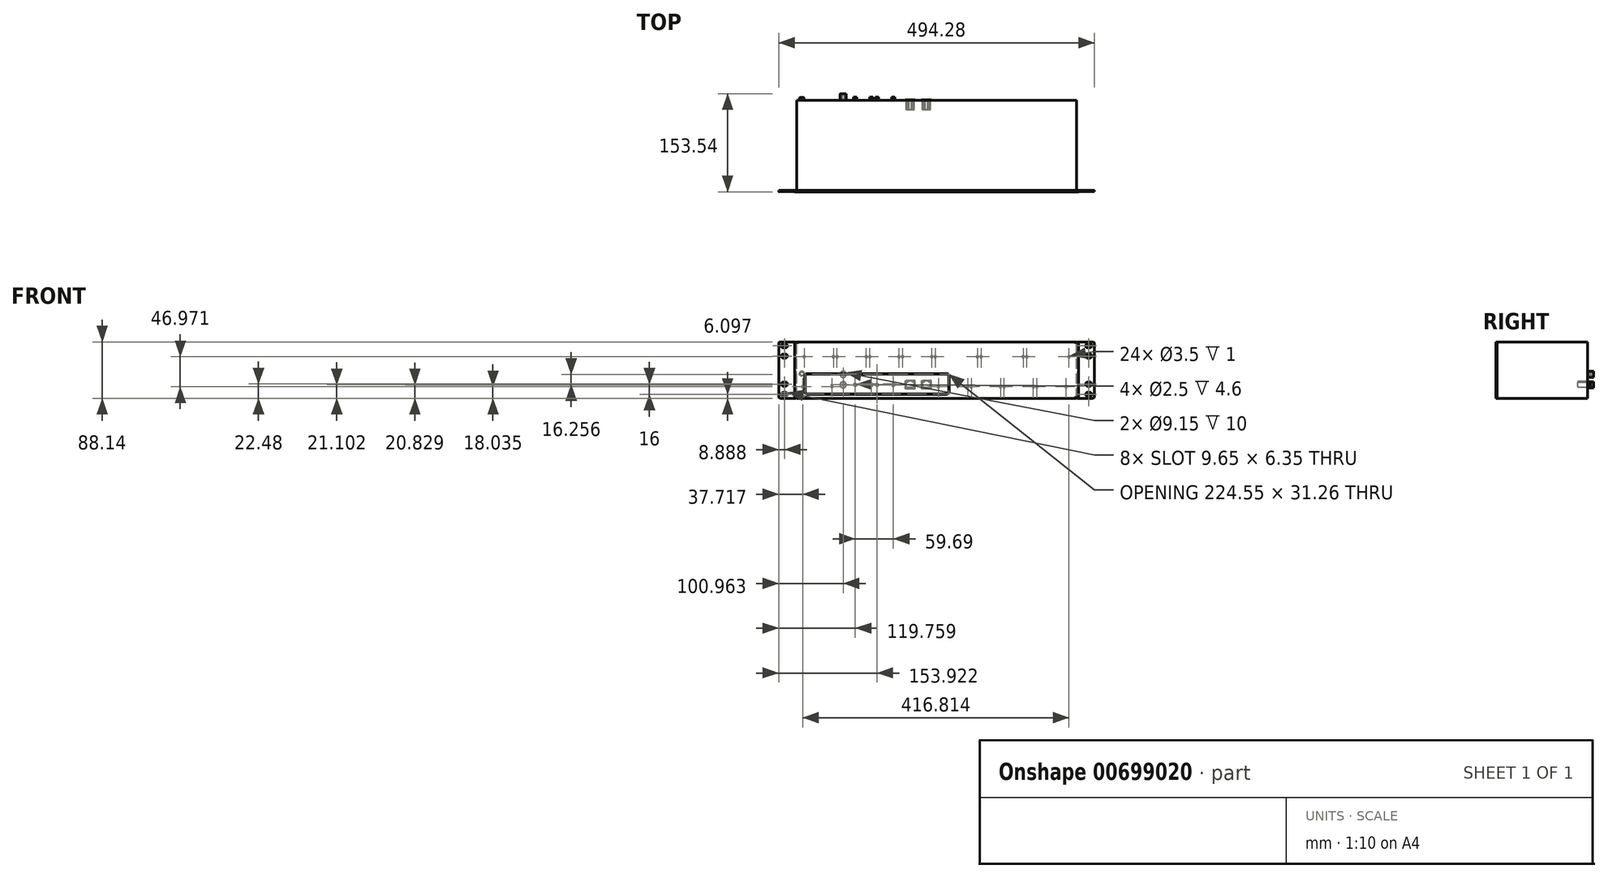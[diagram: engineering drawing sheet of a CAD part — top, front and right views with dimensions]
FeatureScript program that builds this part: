
annotation { "Feature Type Name" : "Feature", "Feature Type Description" : "" }
export const myFeature = defineFeature(function(context is Context, id is Id, definition is map)
    precondition{}
    {
        {
            var Q0;
            Q0=qCreatedBy(makeId("Front.planeOp"),FACE);
            var sketch = newSketch(context, id + "F0", { "sketchPlane" : qUnion([Q0])});
            skLineSegment(sketch, "E0.bottom", {"start": v(222.25, -44.07) * mm, "end": v(-222.25, -44.07) * mm});
            skLineSegment(sketch, "E0.top", {"start": v(222.25, 44.07) * mm, "end": v(-222.25, 44.07) * mm});
            skLineSegment(sketch, "E0.left", {"start": v(222.25, -44.07) * mm, "end": v(222.25, 44.07) * mm});
            skLineSegment(sketch, "E0.right", {"start": v(-222.25, -44.07) * mm, "end": v(-222.25, 44.07) * mm});
            skPoint(sketch, "E0.middle", {"position": v(0, 0) * mm});
            skPoint(sketch, "E1", {"position": v(-215.9, 44.07) * mm});
            skLineSegment(sketch, "E2", {"start": v(-215.9, 44.07) * mm, "end": v(-215.9, 43.3) * mm});
            skLineSegment(sketch, "E3", {"start": v(-215.9, 43.3) * mm, "end": v(-222.25, 43.3) * mm});
            skPoint(sketch, "E4.MirrorP", {"position": v(215.9, 44.07) * mm});
            skLineSegment(sketch, "E5.MirrorCS", {"start": v(215.9, 43.3) * mm, "end": v(222.25, 43.3) * mm});
            skLineSegment(sketch, "E6.MirrorCS", {"start": v(215.9, 44.07) * mm, "end": v(215.9, 43.3) * mm});
            skLineSegment(sketch, "E7.MirrorCS", {"start": v(-215.9, -44.07) * mm, "end": v(-215.9, -43.3) * mm});
            skLineSegment(sketch, "E8.MirrorCS", {"start": v(215.9, -44.07) * mm, "end": v(215.9, -43.3) * mm});
            skLineSegment(sketch, "E9.MirrorCS", {"start": v(-215.9, -43.3) * mm, "end": v(-222.25, -43.3) * mm});
            skLineSegment(sketch, "E10.MirrorCS", {"start": v(215.9, -43.3) * mm, "end": v(222.25, -43.3) * mm});
            skPoint(sketch, "E11.MirrorP", {"position": v(215.9, -44.07) * mm});
            skPoint(sketch, "E12.MirrorP", {"position": v(-215.9, -44.07) * mm});
            skPoint(sketch, "E13", {"position": v(-220.47, -44.07) * mm});
            skPoint(sketch, "E14", {"position": v(-220.47, 44.07) * mm});
            skLineSegment(sketch, "E15", {"start": v(-220.47, 44.07) * mm, "end": v(-247.14, 44.07) * mm});
            skLineSegment(sketch, "E16", {"start": v(-247.14, 44.07) * mm, "end": v(-247.14, -44.07) * mm});
            skLineSegment(sketch, "E17", {"start": v(-247.14, -44.07) * mm, "end": v(-220.47, -44.07) * mm});
            skPoint(sketch, "E18.MirrorP", {"position": v(220.47, 44.07) * mm});
            skLineSegment(sketch, "E19.MirrorCS", {"start": v(220.47, 44.07) * mm, "end": v(247.14, 44.07) * mm});
            skLineSegment(sketch, "E20.MirrorCS", {"start": v(247.14, 44.07) * mm, "end": v(247.14, -44.07) * mm});
            skLineSegment(sketch, "E21.MirrorCS", {"start": v(247.14, -44.07) * mm, "end": v(220.47, -44.07) * mm});
            skPoint(sketch, "E22.MirrorP", {"position": v(220.47, -44.07) * mm});
            skLineSegment(sketch, "E23", {"start": v(-220.47, 44.07) * mm, "end": v(-220.47, -44.07) * mm});
            skLineSegment(sketch, "E24", {"start": v(220.47, 44.07) * mm, "end": v(220.47, -44.07) * mm});
            skSolve(sketch);
        }
        {
            var Q0;
            {var subQ5=sQuery(id+"F0.wireOp",EDGE,"E2");Q0=makeQuery(id+"F0.imprint","IMPRINT",FACE,{"disambiguationData":[TD([[makeQuery(id+"F0.imprint","IMPRINT",EDGE,{"derivedFrom":subQ5}),1.0]])]});}
            var Q1;
            {var subQ0=sQuery(id+"F0.wireOp",EDGE,"E3");var subQ1=sQuery(id+"F0.wireOp",EDGE,"E0.right");var subQ2=makeQuery(id+"F0.imprint","INTERSECT",VERTEX,{"derivedFrom":[subQ1,subQ0]});Q1=makeQuery(id+"F0.imprint","IMPRINT",FACE,{"disambiguationData":[TD([[makeQuery(id+"F0.imprint","IMPRINT",EDGE,{"disambiguationData":[TD([[subQ2,1.0]])],"derivedFrom":subQ1}),-1.0]])]});}
            var Q2;
            {var subQ0=sQuery(id+"F0.wireOp",EDGE,"E5.MirrorCS");var subQ1=sQuery(id+"F0.wireOp",EDGE,"E0.left");var subQ2=makeQuery(id+"F0.imprint","INTERSECT",VERTEX,{"derivedFrom":[subQ1,subQ0]});Q2=makeQuery(id+"F0.imprint","IMPRINT",FACE,{"disambiguationData":[TD([[makeQuery(id+"F0.imprint","IMPRINT",EDGE,{"disambiguationData":[TD([[subQ2,1.0]])],"derivedFrom":subQ1}),1.0]])]});}
            extrude(context, id + "F1", {"entities" : qUnion([Q0, Q1, Q2]), "depth" : 2 * mm, "offsetDistance" : 25 * mm});
        }
        {
            var Q0;
            Q0=makeQuery(id+"F1.opExtrude","SWEPT_EDGE",EDGE,{"disambiguationData":[OSD([sQuery(id+"F0.wireOp",EDGE,"E0.right"),sQuery(id+"F0.wireOp",EDGE,"E3")])]});
            var Q1;
            Q1=makeQuery(id+"F1.opExtrude","SWEPT_EDGE",EDGE,{"disambiguationData":[OSD([sQuery(id+"F0.wireOp",EDGE,"E0.right"),sQuery(id+"F0.wireOp",EDGE,"E9.MirrorCS")])]});
            var Q2;
            Q2=makeQuery(id+"F1.opExtrude","SWEPT_EDGE",EDGE,{"disambiguationData":[OSD([sQuery(id+"F0.wireOp",EDGE,"E0.left"),sQuery(id+"F0.wireOp",EDGE,"E10.MirrorCS")])]});
            var Q3;
            Q3=makeQuery(id+"F1.opExtrude","SWEPT_EDGE",EDGE,{"disambiguationData":[OSD([sQuery(id+"F0.wireOp",EDGE,"E0.left"),sQuery(id+"F0.wireOp",EDGE,"E5.MirrorCS")])]});
            fillet(context, id + "F2", {"entities" : qUnion([Q0, Q1, Q2, Q3]), "radius" : 3 * mm, "tangentPropagation" : true, "allowEdgeOverflow" : false});
        }
        {
            var Q0;
            {var subQ3=sQuery(id+"F0.wireOp",EDGE,"E16");Q0=makeQuery(id+"F0.imprint","IMPRINT",FACE,{"disambiguationData":[TD([[makeQuery(id+"F0.imprint","IMPRINT",EDGE,{"derivedFrom":subQ3}),1.0]])]});}
            var Q1;
            {var subQ0=sQuery(id+"F0.wireOp",EDGE,"E15");var subQ1=sQuery(id+"F0.wireOp",EDGE,"E0.right");var subQ2=makeQuery(id+"F0.imprint","INTERSECT",VERTEX,{"derivedFrom":[subQ1,subQ0]});Q1=makeQuery(id+"F0.imprint","IMPRINT",FACE,{"disambiguationData":[TD([[makeQuery(id+"F0.imprint","IMPRINT",EDGE,{"disambiguationData":[TD([[subQ2,1.0]])],"derivedFrom":subQ1}),-1.0]])]});}
            var Q2;
            {var subQ0=sQuery(id+"F0.wireOp",EDGE,"E3");var subQ1=sQuery(id+"F0.wireOp",EDGE,"E0.right");var subQ2=makeQuery(id+"F0.imprint","INTERSECT",VERTEX,{"derivedFrom":[subQ1,subQ0]});Q2=makeQuery(id+"F0.imprint","IMPRINT",FACE,{"disambiguationData":[TD([[makeQuery(id+"F0.imprint","IMPRINT",EDGE,{"disambiguationData":[TD([[subQ2,1.0]])],"derivedFrom":subQ1}),-1.0]])]});}
            var Q3;
            {var subQ0=sQuery(id+"F0.wireOp",EDGE,"E17");var subQ1=sQuery(id+"F0.wireOp",EDGE,"E0.right");var subQ2=makeQuery(id+"F0.imprint","INTERSECT",VERTEX,{"derivedFrom":[subQ1,subQ0]});Q3=makeQuery(id+"F0.imprint","IMPRINT",FACE,{"disambiguationData":[TD([[makeQuery(id+"F0.imprint","IMPRINT",EDGE,{"disambiguationData":[TD([[subQ2,-1.0]])],"derivedFrom":subQ1}),-1.0]])]});}
            var Q4;
            {var subQ3=sQuery(id+"F0.wireOp",EDGE,"E20.MirrorCS");Q4=makeQuery(id+"F0.imprint","IMPRINT",FACE,{"disambiguationData":[TD([[makeQuery(id+"F0.imprint","IMPRINT",EDGE,{"derivedFrom":subQ3}),-1.0]])]});}
            var Q5;
            {var subQ0=sQuery(id+"F0.wireOp",EDGE,"E19.MirrorCS");var subQ1=sQuery(id+"F0.wireOp",EDGE,"E0.left");var subQ2=makeQuery(id+"F0.imprint","INTERSECT",VERTEX,{"derivedFrom":[subQ1,subQ0]});Q5=makeQuery(id+"F0.imprint","IMPRINT",FACE,{"disambiguationData":[TD([[makeQuery(id+"F0.imprint","IMPRINT",EDGE,{"disambiguationData":[TD([[subQ2,1.0]])],"derivedFrom":subQ1}),1.0]])]});}
            var Q6;
            {var subQ0=sQuery(id+"F0.wireOp",EDGE,"E5.MirrorCS");var subQ1=sQuery(id+"F0.wireOp",EDGE,"E0.left");var subQ2=makeQuery(id+"F0.imprint","INTERSECT",VERTEX,{"derivedFrom":[subQ1,subQ0]});Q6=makeQuery(id+"F0.imprint","IMPRINT",FACE,{"disambiguationData":[TD([[makeQuery(id+"F0.imprint","IMPRINT",EDGE,{"disambiguationData":[TD([[subQ2,1.0]])],"derivedFrom":subQ1}),1.0]])]});}
            var Q7;
            {var subQ0=sQuery(id+"F0.wireOp",EDGE,"E21.MirrorCS");var subQ1=sQuery(id+"F0.wireOp",EDGE,"E0.left");var subQ2=makeQuery(id+"F0.imprint","INTERSECT",VERTEX,{"derivedFrom":[subQ1,subQ0]});Q7=makeQuery(id+"F0.imprint","IMPRINT",FACE,{"disambiguationData":[TD([[makeQuery(id+"F0.imprint","IMPRINT",EDGE,{"disambiguationData":[TD([[subQ2,-1.0]])],"derivedFrom":subQ1}),1.0]])]});}
            extrude(context, id + "F3", {"entities" : qUnion([Q0, Q1, Q2, Q3, Q4, Q5, Q6, Q7]), "depth" : 1.9 * mm, "offsetDistance" : 25 * mm});
        }
        {
            var Q0;
            Q0=makeQuery(id+"F3.opExtrude","SWEPT_EDGE",EDGE,{"disambiguationData":[OSD([sQuery(id+"F0.wireOp",EDGE,"E15"),sQuery(id+"F0.wireOp",EDGE,"E16")])]});
            var Q1;
            Q1=makeQuery(id+"F3.opExtrude","SWEPT_EDGE",EDGE,{"disambiguationData":[OSD([sQuery(id+"F0.wireOp",EDGE,"E16"),sQuery(id+"F0.wireOp",EDGE,"E17")])]});
            var Q2;
            Q2=makeQuery(id+"F3.opExtrude","SWEPT_EDGE",EDGE,{"disambiguationData":[OSD([sQuery(id+"F0.wireOp",EDGE,"E20.MirrorCS"),sQuery(id+"F0.wireOp",EDGE,"E21.MirrorCS")])]});
            var Q3;
            Q3=makeQuery(id+"F3.opExtrude","SWEPT_EDGE",EDGE,{"disambiguationData":[OSD([sQuery(id+"F0.wireOp",EDGE,"E19.MirrorCS"),sQuery(id+"F0.wireOp",EDGE,"E20.MirrorCS")])]});
            fillet(context, id + "F4", {"entities" : qUnion([Q0, Q1, Q2, Q3]), "radius" : 2.5 * mm, "tangentPropagation" : true, "allowEdgeOverflow" : false});
        }
        {
            var Q0;
            Q0=makeQuery(id+"F3.opExtrude","CAP_FACE",FACE,{"disambiguationData":[OSD([sQuery(id+"F0.wireOp",EDGE,"E15"),sQuery(id+"F0.wireOp",EDGE,"E16"),sQuery(id+"F0.wireOp",EDGE,"E17"),sQuery(id+"F0.wireOp",EDGE,"E23")])],"isStart":false});
            var sketch = newSketch(context, id + "F5", { "sketchPlane" : qUnion([Q0])});
            skLineSegment(sketch, "E25", {"start": v(-239.9, -41.15) * mm, "end": v(-236.6, -41.15) * mm});
            skLineSegment(sketch, "E26", {"start": v(-236.6, -41.15) * mm, "end": v(-236.6, -34.8) * mm});
            skLineSegment(sketch, "E27", {"start": v(-236.6, -34.8) * mm, "end": v(-239.9, -34.8) * mm});
            skLineSegment(sketch, "E28", {"start": v(-239.9, -34.8) * mm, "end": v(-239.9, -41.15) * mm});
            skLineSegment(sketch, "E29", {"start": v(-239.9, -37.97) * mm, "end": v(-243.08, -37.97) * mm});
            skLineSegment(sketch, "E30", {"start": v(-236.6, -37.97) * mm, "end": v(-233.43, -37.97) * mm});
            skArc(sketch, "E31", {"start": v(-239.9, -34.8) * mm, "mid": v(-243.08, -37.97) * mm, "end": v(-239.9, -41.15) * mm});
            skArc(sketch, "E32", {"start": v(-236.6, -41.15) * mm, "mid": v(-233.43, -37.97) * mm, "end": v(-236.6, -34.8) * mm});
            skPoint(sketch, "E33", {"position": v(-238.25, -34.8) * mm});
            skLineSegment(sketch, "E34.0.1.0", {"start": v(-239.9, -18.8) * mm, "end": v(-239.9, -25.15) * mm});
            skLineSegment(sketch, "E34.0.1.1", {"start": v(-239.9, -21.97) * mm, "end": v(-243.08, -21.97) * mm});
            skLineSegment(sketch, "E34.0.1.2", {"start": v(-236.6, -21.97) * mm, "end": v(-233.43, -21.97) * mm});
            skArc(sketch, "E34.0.1.3", {"start": v(-239.9, -18.8) * mm, "mid": v(-243.08, -21.97) * mm, "end": v(-239.9, -25.15) * mm});
            skArc(sketch, "E34.0.1.4", {"start": v(-236.6, -25.15) * mm, "mid": v(-233.43, -21.97) * mm, "end": v(-236.6, -18.8) * mm});
            skLineSegment(sketch, "E34.0.1.5", {"start": v(-236.6, -25.15) * mm, "end": v(-236.6, -18.8) * mm});
            skLineSegment(sketch, "E34.0.1.6", {"start": v(-239.9, -25.15) * mm, "end": v(-236.6, -25.15) * mm});
            skPoint(sketch, "E34.0.1.7", {"position": v(-238.25, -18.8) * mm});
            skLineSegment(sketch, "E34.0.1.8", {"start": v(-236.6, -18.8) * mm, "end": v(-239.9, -18.8) * mm});
            skLineSegment(sketch, "E34.direction1", {"start": v(-239.9, -41.15) * mm, "end": v(-214.9, -41.15) * mm, "construction": true});
            skLineSegment(sketch, "E34.direction2", {"start": v(-239.9, -41.15) * mm, "end": v(-239.9, -25.15) * mm, "construction": true});
            skLineSegment(sketch, "E35.MirrorCS", {"start": v(-236.6, 21.97) * mm, "end": v(-233.43, 21.97) * mm});
            skLineSegment(sketch, "E36.MirrorCS", {"start": v(-239.9, 21.97) * mm, "end": v(-243.08, 21.97) * mm});
            skLineSegment(sketch, "E37.MirrorCS", {"start": v(-239.9, 18.8) * mm, "end": v(-239.9, 25.15) * mm});
            skLineSegment(sketch, "E38.MirrorCS", {"start": v(-236.6, 37.97) * mm, "end": v(-233.43, 37.97) * mm});
            skLineSegment(sketch, "E39.MirrorCS", {"start": v(-236.6, 18.8) * mm, "end": v(-239.9, 18.8) * mm});
            skLineSegment(sketch, "E40.MirrorCS", {"start": v(-239.9, 37.97) * mm, "end": v(-243.08, 37.97) * mm});
            skLineSegment(sketch, "E41.MirrorCS", {"start": v(-239.9, 41.15) * mm, "end": v(-236.6, 41.15) * mm});
            skLineSegment(sketch, "E42.MirrorCS", {"start": v(-236.6, 34.8) * mm, "end": v(-239.9, 34.8) * mm});
            skLineSegment(sketch, "E43.MirrorCS", {"start": v(-239.9, 34.8) * mm, "end": v(-239.9, 41.15) * mm});
            skLineSegment(sketch, "E44.MirrorCS", {"start": v(-236.6, 41.15) * mm, "end": v(-236.6, 34.8) * mm});
            skLineSegment(sketch, "E45.MirrorCS", {"start": v(-239.9, 41.15) * mm, "end": v(-239.9, 25.15) * mm, "construction": true});
            skPoint(sketch, "E46.MirrorP", {"position": v(-238.25, 18.8) * mm});
            skArc(sketch, "E47.MirrorCS", {"start": v(-236.6, 25.15) * mm, "mid": v(-233.43, 21.97) * mm, "end": v(-236.6, 18.8) * mm});
            skArc(sketch, "E48.MirrorCS", {"start": v(-239.9, 18.8) * mm, "mid": v(-243.08, 21.97) * mm, "end": v(-239.9, 25.15) * mm});
            skArc(sketch, "E49.MirrorCS", {"start": v(-236.6, 41.15) * mm, "mid": v(-233.43, 37.97) * mm, "end": v(-236.6, 34.8) * mm});
            skPoint(sketch, "E50.MirrorP", {"position": v(-238.25, 34.8) * mm});
            skArc(sketch, "E51.MirrorCS", {"start": v(-239.9, 34.8) * mm, "mid": v(-243.08, 37.97) * mm, "end": v(-239.9, 41.15) * mm});
            skLineSegment(sketch, "E52.MirrorCS", {"start": v(-236.6, 25.15) * mm, "end": v(-236.6, 18.8) * mm});
            skLineSegment(sketch, "E53.MirrorCS", {"start": v(-239.9, 25.15) * mm, "end": v(-236.6, 25.15) * mm});
            skLineSegment(sketch, "E54.MirrorCS", {"start": v(236.6, -41.15) * mm, "end": v(236.6, -34.8) * mm});
            skLineSegment(sketch, "E55.MirrorCS", {"start": v(236.6, -34.8) * mm, "end": v(239.9, -34.8) * mm});
            skLineSegment(sketch, "E56.MirrorCS", {"start": v(239.9, -34.8) * mm, "end": v(239.9, -41.15) * mm});
            skLineSegment(sketch, "E57.MirrorCS", {"start": v(239.9, -37.97) * mm, "end": v(243.08, -37.97) * mm});
            skPoint(sketch, "E58.MirrorP", {"position": v(238.25, -34.8) * mm});
            skLineSegment(sketch, "E59.MirrorCS", {"start": v(236.6, -37.97) * mm, "end": v(233.43, -37.97) * mm});
            skLineSegment(sketch, "E60.MirrorCS", {"start": v(239.9, -41.15) * mm, "end": v(236.6, -41.15) * mm});
            skArc(sketch, "E61.MirrorCS", {"start": v(239.9, -34.8) * mm, "mid": v(243.08, -37.97) * mm, "end": v(239.9, -41.15) * mm});
            skArc(sketch, "E62.MirrorCS", {"start": v(236.6, -41.15) * mm, "mid": v(233.43, -37.97) * mm, "end": v(236.6, -34.8) * mm});
            skArc(sketch, "E63.0.1.0", {"start": v(236.6, -25.15) * mm, "mid": v(233.43, -21.97) * mm, "end": v(236.6, -18.8) * mm});
            skLineSegment(sketch, "E63.0.1.1", {"start": v(239.9, -21.97) * mm, "end": v(243.08, -21.97) * mm});
            skLineSegment(sketch, "E63.0.1.2", {"start": v(239.9, -18.8) * mm, "end": v(239.9, -25.15) * mm});
            skLineSegment(sketch, "E63.0.1.3", {"start": v(236.6, -25.15) * mm, "end": v(236.6, -18.8) * mm});
            skArc(sketch, "E63.0.1.4", {"start": v(239.9, -18.8) * mm, "mid": v(243.08, -21.97) * mm, "end": v(239.9, -25.15) * mm});
            skPoint(sketch, "E63.0.1.5", {"position": v(238.25, -18.8) * mm});
            skLineSegment(sketch, "E63.0.1.6", {"start": v(239.9, -25.15) * mm, "end": v(236.6, -25.15) * mm});
            skLineSegment(sketch, "E63.0.1.7", {"start": v(236.6, -21.97) * mm, "end": v(233.43, -21.97) * mm});
            skLineSegment(sketch, "E63.0.1.8", {"start": v(236.6, -18.8) * mm, "end": v(239.9, -18.8) * mm});
            skLineSegment(sketch, "E63.direction1", {"start": v(236.6, -41.15) * mm, "end": v(261.6, -41.15) * mm, "construction": true});
            skLineSegment(sketch, "E63.direction2", {"start": v(236.6, -41.15) * mm, "end": v(236.6, -25.15) * mm, "construction": true});
            skLineSegment(sketch, "E64.MirrorCS", {"start": v(236.6, 34.8) * mm, "end": v(239.9, 34.8) * mm});
            skLineSegment(sketch, "E65.MirrorCS", {"start": v(236.6, 18.8) * mm, "end": v(239.9, 18.8) * mm});
            skLineSegment(sketch, "E66.MirrorCS", {"start": v(236.6, 41.15) * mm, "end": v(236.6, 34.8) * mm});
            skArc(sketch, "E67.MirrorCS", {"start": v(239.9, 18.8) * mm, "mid": v(243.08, 21.97) * mm, "end": v(239.9, 25.15) * mm});
            skLineSegment(sketch, "E68.MirrorCS", {"start": v(239.9, 37.97) * mm, "end": v(243.08, 37.97) * mm});
            skLineSegment(sketch, "E69.MirrorCS", {"start": v(236.6, 41.15) * mm, "end": v(236.6, 25.15) * mm, "construction": true});
            skLineSegment(sketch, "E70.MirrorCS", {"start": v(239.9, 18.8) * mm, "end": v(239.9, 25.15) * mm});
            skArc(sketch, "E71.MirrorCS", {"start": v(239.9, 34.8) * mm, "mid": v(243.08, 37.97) * mm, "end": v(239.9, 41.15) * mm});
            skLineSegment(sketch, "E72.MirrorCS", {"start": v(239.9, 34.8) * mm, "end": v(239.9, 41.15) * mm});
            skArc(sketch, "E73.MirrorCS", {"start": v(236.6, 25.15) * mm, "mid": v(233.43, 21.97) * mm, "end": v(236.6, 18.8) * mm});
            skLineSegment(sketch, "E74.MirrorCS", {"start": v(239.9, 21.97) * mm, "end": v(243.08, 21.97) * mm});
            skLineSegment(sketch, "E75.MirrorCS", {"start": v(236.6, 25.15) * mm, "end": v(236.6, 18.8) * mm});
            skPoint(sketch, "E76.MirrorP", {"position": v(238.25, 18.8) * mm});
            skPoint(sketch, "E77.MirrorP", {"position": v(238.25, 34.8) * mm});
            skLineSegment(sketch, "E78.MirrorCS", {"start": v(236.6, 21.97) * mm, "end": v(233.43, 21.97) * mm});
            skLineSegment(sketch, "E79.MirrorCS", {"start": v(239.9, 41.15) * mm, "end": v(236.6, 41.15) * mm});
            skArc(sketch, "E80.MirrorCS", {"start": v(236.6, 41.15) * mm, "mid": v(233.43, 37.97) * mm, "end": v(236.6, 34.8) * mm});
            skLineSegment(sketch, "E81.MirrorCS", {"start": v(239.9, 25.15) * mm, "end": v(236.6, 25.15) * mm});
            skLineSegment(sketch, "E82.MirrorCS", {"start": v(236.6, 37.97) * mm, "end": v(233.43, 37.97) * mm});
            skSolve(sketch);
        }
        {
            var Q0;
            {var subQ0=sQuery(id+"F5.wireOp",EDGE,"E40.MirrorCS");Q0=makeQuery(id+"F5.imprint","IMPRINT",FACE,{"disambiguationData":[TD([[makeQuery(id+"F5.imprint","IMPRINT",EDGE,{"derivedFrom":subQ0}),-1.0]])]});}
            var Q1;
            {var subQ0=sQuery(id+"F5.wireOp",EDGE,"E40.MirrorCS");Q1=makeQuery(id+"F5.imprint","IMPRINT",FACE,{"disambiguationData":[TD([[makeQuery(id+"F5.imprint","IMPRINT",EDGE,{"derivedFrom":subQ0}),1.0]])]});}
            var Q2;
            {var subQ3=sQuery(id+"F5.wireOp",EDGE,"E41.MirrorCS");Q2=makeQuery(id+"F5.imprint","IMPRINT",FACE,{"disambiguationData":[TD([[makeQuery(id+"F5.imprint","IMPRINT",EDGE,{"derivedFrom":subQ3}),-1.0]])]});}
            var Q3;
            {var subQ0=sQuery(id+"F5.wireOp",EDGE,"E38.MirrorCS");Q3=makeQuery(id+"F5.imprint","IMPRINT",FACE,{"disambiguationData":[TD([[makeQuery(id+"F5.imprint","IMPRINT",EDGE,{"derivedFrom":subQ0}),-1.0]])]});}
            var Q4;
            {var subQ0=sQuery(id+"F5.wireOp",EDGE,"E38.MirrorCS");Q4=makeQuery(id+"F5.imprint","IMPRINT",FACE,{"disambiguationData":[TD([[makeQuery(id+"F5.imprint","IMPRINT",EDGE,{"derivedFrom":subQ0}),1.0]])]});}
            var Q5;
            {var subQ0=sQuery(id+"F5.wireOp",EDGE,"E36.MirrorCS");Q5=makeQuery(id+"F5.imprint","IMPRINT",FACE,{"disambiguationData":[TD([[makeQuery(id+"F5.imprint","IMPRINT",EDGE,{"derivedFrom":subQ0}),-1.0]])]});}
            var Q6;
            {var subQ0=sQuery(id+"F5.wireOp",EDGE,"E36.MirrorCS");Q6=makeQuery(id+"F5.imprint","IMPRINT",FACE,{"disambiguationData":[TD([[makeQuery(id+"F5.imprint","IMPRINT",EDGE,{"derivedFrom":subQ0}),1.0]])]});}
            var Q7;
            {var subQ4=sQuery(id+"F5.wireOp",EDGE,"E39.MirrorCS");Q7=makeQuery(id+"F5.imprint","IMPRINT",FACE,{"disambiguationData":[TD([[makeQuery(id+"F5.imprint","IMPRINT",EDGE,{"derivedFrom":subQ4}),-1.0]])]});}
            var Q8;
            {var subQ0=sQuery(id+"F5.wireOp",EDGE,"E35.MirrorCS");Q8=makeQuery(id+"F5.imprint","IMPRINT",FACE,{"disambiguationData":[TD([[makeQuery(id+"F5.imprint","IMPRINT",EDGE,{"derivedFrom":subQ0}),-1.0]])]});}
            var Q9;
            {var subQ0=sQuery(id+"F5.wireOp",EDGE,"E35.MirrorCS");Q9=makeQuery(id+"F5.imprint","IMPRINT",FACE,{"disambiguationData":[TD([[makeQuery(id+"F5.imprint","IMPRINT",EDGE,{"derivedFrom":subQ0}),1.0]])]});}
            var Q10;
            {var subQ3=sQuery(id+"F5.wireOp",EDGE,"E29");Q10=makeQuery(id+"F5.imprint","IMPRINT",FACE,{"disambiguationData":[TD([[makeQuery(id+"F5.imprint","IMPRINT",EDGE,{"derivedFrom":subQ3}),-1.0]])]});}
            var Q11;
            {var subQ3=sQuery(id+"F5.wireOp",EDGE,"E29");Q11=makeQuery(id+"F5.imprint","IMPRINT",FACE,{"disambiguationData":[TD([[makeQuery(id+"F5.imprint","IMPRINT",EDGE,{"derivedFrom":subQ3}),1.0]])]});}
            var Q12;
            {var subQ4=sQuery(id+"F5.wireOp",EDGE,"E25");Q12=makeQuery(id+"F5.imprint","IMPRINT",FACE,{"disambiguationData":[TD([[makeQuery(id+"F5.imprint","IMPRINT",EDGE,{"derivedFrom":subQ4}),1.0]])]});}
            var Q13;
            {var subQ3=sQuery(id+"F5.wireOp",EDGE,"E30");Q13=makeQuery(id+"F5.imprint","IMPRINT",FACE,{"disambiguationData":[TD([[makeQuery(id+"F5.imprint","IMPRINT",EDGE,{"derivedFrom":subQ3}),-1.0]])]});}
            var Q14;
            {var subQ3=sQuery(id+"F5.wireOp",EDGE,"E30");Q14=makeQuery(id+"F5.imprint","IMPRINT",FACE,{"disambiguationData":[TD([[makeQuery(id+"F5.imprint","IMPRINT",EDGE,{"derivedFrom":subQ3}),1.0]])]});}
            var Q15;
            {var subQ0=sQuery(id+"F5.wireOp",EDGE,"E34.0.1.2");Q15=makeQuery(id+"F5.imprint","IMPRINT",FACE,{"disambiguationData":[TD([[makeQuery(id+"F5.imprint","IMPRINT",EDGE,{"derivedFrom":subQ0}),1.0]])]});}
            var Q16;
            {var subQ0=sQuery(id+"F5.wireOp",EDGE,"E34.0.1.2");Q16=makeQuery(id+"F5.imprint","IMPRINT",FACE,{"disambiguationData":[TD([[makeQuery(id+"F5.imprint","IMPRINT",EDGE,{"derivedFrom":subQ0}),-1.0]])]});}
            var Q17;
            {var subQ4=sQuery(id+"F5.wireOp",EDGE,"E34.0.1.6");Q17=makeQuery(id+"F5.imprint","IMPRINT",FACE,{"disambiguationData":[TD([[makeQuery(id+"F5.imprint","IMPRINT",EDGE,{"derivedFrom":subQ4}),1.0]])]});}
            var Q18;
            {var subQ3=sQuery(id+"F5.wireOp",EDGE,"E34.0.1.1");Q18=makeQuery(id+"F5.imprint","IMPRINT",FACE,{"disambiguationData":[TD([[makeQuery(id+"F5.imprint","IMPRINT",EDGE,{"derivedFrom":subQ3}),1.0]])]});}
            var Q19;
            {var subQ3=sQuery(id+"F5.wireOp",EDGE,"E34.0.1.1");Q19=makeQuery(id+"F5.imprint","IMPRINT",FACE,{"disambiguationData":[TD([[makeQuery(id+"F5.imprint","IMPRINT",EDGE,{"derivedFrom":subQ3}),-1.0]])]});}
            var Q20;
            {var subQ3=sQuery(id+"F5.wireOp",EDGE,"E82.MirrorCS");Q20=makeQuery(id+"F5.imprint","IMPRINT",FACE,{"disambiguationData":[TD([[makeQuery(id+"F5.imprint","IMPRINT",EDGE,{"derivedFrom":subQ3}),-1.0]])]});}
            var Q21;
            {var subQ3=sQuery(id+"F5.wireOp",EDGE,"E82.MirrorCS");Q21=makeQuery(id+"F5.imprint","IMPRINT",FACE,{"disambiguationData":[TD([[makeQuery(id+"F5.imprint","IMPRINT",EDGE,{"derivedFrom":subQ3}),1.0]])]});}
            var Q22;
            {var subQ2=sQuery(id+"F5.wireOp",EDGE,"E64.MirrorCS");Q22=makeQuery(id+"F5.imprint","IMPRINT",FACE,{"disambiguationData":[TD([[makeQuery(id+"F5.imprint","IMPRINT",EDGE,{"derivedFrom":subQ2}),1.0]])]});}
            var Q23;
            {var subQ0=sQuery(id+"F5.wireOp",EDGE,"E68.MirrorCS");Q23=makeQuery(id+"F5.imprint","IMPRINT",FACE,{"disambiguationData":[TD([[makeQuery(id+"F5.imprint","IMPRINT",EDGE,{"derivedFrom":subQ0}),1.0]])]});}
            var Q24;
            {var subQ0=sQuery(id+"F5.wireOp",EDGE,"E68.MirrorCS");Q24=makeQuery(id+"F5.imprint","IMPRINT",FACE,{"disambiguationData":[TD([[makeQuery(id+"F5.imprint","IMPRINT",EDGE,{"derivedFrom":subQ0}),-1.0]])]});}
            var Q25;
            {var subQ3=sQuery(id+"F5.wireOp",EDGE,"E78.MirrorCS");Q25=makeQuery(id+"F5.imprint","IMPRINT",FACE,{"disambiguationData":[TD([[makeQuery(id+"F5.imprint","IMPRINT",EDGE,{"derivedFrom":subQ3}),-1.0]])]});}
            var Q26;
            {var subQ3=sQuery(id+"F5.wireOp",EDGE,"E78.MirrorCS");Q26=makeQuery(id+"F5.imprint","IMPRINT",FACE,{"disambiguationData":[TD([[makeQuery(id+"F5.imprint","IMPRINT",EDGE,{"derivedFrom":subQ3}),1.0]])]});}
            var Q27;
            {var subQ4=sQuery(id+"F5.wireOp",EDGE,"E65.MirrorCS");Q27=makeQuery(id+"F5.imprint","IMPRINT",FACE,{"disambiguationData":[TD([[makeQuery(id+"F5.imprint","IMPRINT",EDGE,{"derivedFrom":subQ4}),1.0]])]});}
            var Q28;
            {var subQ3=sQuery(id+"F5.wireOp",EDGE,"E74.MirrorCS");Q28=makeQuery(id+"F5.imprint","IMPRINT",FACE,{"disambiguationData":[TD([[makeQuery(id+"F5.imprint","IMPRINT",EDGE,{"derivedFrom":subQ3}),1.0]])]});}
            var Q29;
            {var subQ3=sQuery(id+"F5.wireOp",EDGE,"E74.MirrorCS");Q29=makeQuery(id+"F5.imprint","IMPRINT",FACE,{"disambiguationData":[TD([[makeQuery(id+"F5.imprint","IMPRINT",EDGE,{"derivedFrom":subQ3}),-1.0]])]});}
            var Q30;
            {var subQ3=sQuery(id+"F5.wireOp",EDGE,"E63.0.1.7");Q30=makeQuery(id+"F5.imprint","IMPRINT",FACE,{"disambiguationData":[TD([[makeQuery(id+"F5.imprint","IMPRINT",EDGE,{"derivedFrom":subQ3}),-1.0]])]});}
            var Q31;
            {var subQ3=sQuery(id+"F5.wireOp",EDGE,"E63.0.1.7");Q31=makeQuery(id+"F5.imprint","IMPRINT",FACE,{"disambiguationData":[TD([[makeQuery(id+"F5.imprint","IMPRINT",EDGE,{"derivedFrom":subQ3}),1.0]])]});}
            var Q32;
            {var subQ4=sQuery(id+"F5.wireOp",EDGE,"E63.0.1.6");Q32=makeQuery(id+"F5.imprint","IMPRINT",FACE,{"disambiguationData":[TD([[makeQuery(id+"F5.imprint","IMPRINT",EDGE,{"derivedFrom":subQ4}),-1.0]])]});}
            var Q33;
            {var subQ0=sQuery(id+"F5.wireOp",EDGE,"E63.0.1.1");Q33=makeQuery(id+"F5.imprint","IMPRINT",FACE,{"disambiguationData":[TD([[makeQuery(id+"F5.imprint","IMPRINT",EDGE,{"derivedFrom":subQ0}),1.0]])]});}
            var Q34;
            {var subQ0=sQuery(id+"F5.wireOp",EDGE,"E63.0.1.1");Q34=makeQuery(id+"F5.imprint","IMPRINT",FACE,{"disambiguationData":[TD([[makeQuery(id+"F5.imprint","IMPRINT",EDGE,{"derivedFrom":subQ0}),-1.0]])]});}
            var Q35;
            {var subQ3=sQuery(id+"F5.wireOp",EDGE,"E59.MirrorCS");Q35=makeQuery(id+"F5.imprint","IMPRINT",FACE,{"disambiguationData":[TD([[makeQuery(id+"F5.imprint","IMPRINT",EDGE,{"derivedFrom":subQ3}),-1.0]])]});}
            var Q36;
            {var subQ3=sQuery(id+"F5.wireOp",EDGE,"E59.MirrorCS");Q36=makeQuery(id+"F5.imprint","IMPRINT",FACE,{"disambiguationData":[TD([[makeQuery(id+"F5.imprint","IMPRINT",EDGE,{"derivedFrom":subQ3}),1.0]])]});}
            var Q37;
            {var subQ2=sQuery(id+"F5.wireOp",EDGE,"E55.MirrorCS");Q37=makeQuery(id+"F5.imprint","IMPRINT",FACE,{"disambiguationData":[TD([[makeQuery(id+"F5.imprint","IMPRINT",EDGE,{"derivedFrom":subQ2}),-1.0]])]});}
            var Q38;
            {var subQ3=sQuery(id+"F5.wireOp",EDGE,"E57.MirrorCS");Q38=makeQuery(id+"F5.imprint","IMPRINT",FACE,{"disambiguationData":[TD([[makeQuery(id+"F5.imprint","IMPRINT",EDGE,{"derivedFrom":subQ3}),1.0]])]});}
            var Q39;
            {var subQ3=sQuery(id+"F5.wireOp",EDGE,"E57.MirrorCS");Q39=makeQuery(id+"F5.imprint","IMPRINT",FACE,{"disambiguationData":[TD([[makeQuery(id+"F5.imprint","IMPRINT",EDGE,{"derivedFrom":subQ3}),-1.0]])]});}
            extrude(context, id + "F6", {"entities" : qUnion([Q0, Q1, Q2, Q3, Q4, Q5, Q6, Q7, Q8, Q9, Q10, Q11, Q12, Q13, Q14, Q15, Q16, Q17, Q18, Q19, Q20, Q21, Q22, Q23, Q24, Q25, Q26, Q27, Q28, Q29, Q30, Q31, Q32, Q33, Q34, Q35, Q36, Q37, Q38, Q39]), "operationType" : NewBodyOperationType.REMOVE, "endBound" : BoundingType.THROUGH_ALL, "oppositeDirection" : true, "depth" : 25 * mm, "offsetDistance" : 25 * mm});
        }
        {
            var Q0;
            {var subQ4=sQuery(id+"F5.wireOp",EDGE,"E63.0.1.6");Q0=makeQuery(id+"F5.imprint","IMPRINT",FACE,{"disambiguationData":[TD([[makeQuery(id+"F5.imprint","IMPRINT",EDGE,{"derivedFrom":subQ4}),-1.0]])]});}
            var Q1;
            {var subQ3=sQuery(id+"F5.wireOp",EDGE,"E63.0.1.7");Q1=makeQuery(id+"F5.imprint","IMPRINT",FACE,{"disambiguationData":[TD([[makeQuery(id+"F5.imprint","IMPRINT",EDGE,{"derivedFrom":subQ3}),-1.0]])]});}
            var Q2;
            {var subQ3=sQuery(id+"F5.wireOp",EDGE,"E63.0.1.7");Q2=makeQuery(id+"F5.imprint","IMPRINT",FACE,{"disambiguationData":[TD([[makeQuery(id+"F5.imprint","IMPRINT",EDGE,{"derivedFrom":subQ3}),1.0]])]});}
            var Q3;
            {var subQ0=sQuery(id+"F5.wireOp",EDGE,"E63.0.1.1");Q3=makeQuery(id+"F5.imprint","IMPRINT",FACE,{"disambiguationData":[TD([[makeQuery(id+"F5.imprint","IMPRINT",EDGE,{"derivedFrom":subQ0}),-1.0]])]});}
            var Q4;
            {var subQ0=sQuery(id+"F5.wireOp",EDGE,"E63.0.1.1");Q4=makeQuery(id+"F5.imprint","IMPRINT",FACE,{"disambiguationData":[TD([[makeQuery(id+"F5.imprint","IMPRINT",EDGE,{"derivedFrom":subQ0}),1.0]])]});}
            var Q5;
            {var subQ3=sQuery(id+"F5.wireOp",EDGE,"E59.MirrorCS");Q5=makeQuery(id+"F5.imprint","IMPRINT",FACE,{"disambiguationData":[TD([[makeQuery(id+"F5.imprint","IMPRINT",EDGE,{"derivedFrom":subQ3}),-1.0]])]});}
            var Q6;
            {var subQ3=sQuery(id+"F5.wireOp",EDGE,"E59.MirrorCS");Q6=makeQuery(id+"F5.imprint","IMPRINT",FACE,{"disambiguationData":[TD([[makeQuery(id+"F5.imprint","IMPRINT",EDGE,{"derivedFrom":subQ3}),1.0]])]});}
            var Q7;
            {var subQ2=sQuery(id+"F5.wireOp",EDGE,"E55.MirrorCS");Q7=makeQuery(id+"F5.imprint","IMPRINT",FACE,{"disambiguationData":[TD([[makeQuery(id+"F5.imprint","IMPRINT",EDGE,{"derivedFrom":subQ2}),-1.0]])]});}
            var Q8;
            {var subQ3=sQuery(id+"F5.wireOp",EDGE,"E57.MirrorCS");Q8=makeQuery(id+"F5.imprint","IMPRINT",FACE,{"disambiguationData":[TD([[makeQuery(id+"F5.imprint","IMPRINT",EDGE,{"derivedFrom":subQ3}),1.0]])]});}
            var Q9;
            {var subQ3=sQuery(id+"F5.wireOp",EDGE,"E57.MirrorCS");Q9=makeQuery(id+"F5.imprint","IMPRINT",FACE,{"disambiguationData":[TD([[makeQuery(id+"F5.imprint","IMPRINT",EDGE,{"derivedFrom":subQ3}),-1.0]])]});}
            var Q10;
            {var subQ3=sQuery(id+"F5.wireOp",EDGE,"E78.MirrorCS");Q10=makeQuery(id+"F5.imprint","IMPRINT",FACE,{"disambiguationData":[TD([[makeQuery(id+"F5.imprint","IMPRINT",EDGE,{"derivedFrom":subQ3}),-1.0]])]});}
            var Q11;
            {var subQ3=sQuery(id+"F5.wireOp",EDGE,"E78.MirrorCS");Q11=makeQuery(id+"F5.imprint","IMPRINT",FACE,{"disambiguationData":[TD([[makeQuery(id+"F5.imprint","IMPRINT",EDGE,{"derivedFrom":subQ3}),1.0]])]});}
            var Q12;
            {var subQ4=sQuery(id+"F5.wireOp",EDGE,"E65.MirrorCS");Q12=makeQuery(id+"F5.imprint","IMPRINT",FACE,{"disambiguationData":[TD([[makeQuery(id+"F5.imprint","IMPRINT",EDGE,{"derivedFrom":subQ4}),1.0]])]});}
            var Q13;
            {var subQ3=sQuery(id+"F5.wireOp",EDGE,"E74.MirrorCS");Q13=makeQuery(id+"F5.imprint","IMPRINT",FACE,{"disambiguationData":[TD([[makeQuery(id+"F5.imprint","IMPRINT",EDGE,{"derivedFrom":subQ3}),1.0]])]});}
            var Q14;
            {var subQ3=sQuery(id+"F5.wireOp",EDGE,"E74.MirrorCS");Q14=makeQuery(id+"F5.imprint","IMPRINT",FACE,{"disambiguationData":[TD([[makeQuery(id+"F5.imprint","IMPRINT",EDGE,{"derivedFrom":subQ3}),-1.0]])]});}
            var Q15;
            {var subQ0=sQuery(id+"F5.wireOp",EDGE,"E68.MirrorCS");Q15=makeQuery(id+"F5.imprint","IMPRINT",FACE,{"disambiguationData":[TD([[makeQuery(id+"F5.imprint","IMPRINT",EDGE,{"derivedFrom":subQ0}),1.0]])]});}
            var Q16;
            {var subQ0=sQuery(id+"F5.wireOp",EDGE,"E68.MirrorCS");Q16=makeQuery(id+"F5.imprint","IMPRINT",FACE,{"disambiguationData":[TD([[makeQuery(id+"F5.imprint","IMPRINT",EDGE,{"derivedFrom":subQ0}),-1.0]])]});}
            var Q17;
            {var subQ2=sQuery(id+"F5.wireOp",EDGE,"E64.MirrorCS");Q17=makeQuery(id+"F5.imprint","IMPRINT",FACE,{"disambiguationData":[TD([[makeQuery(id+"F5.imprint","IMPRINT",EDGE,{"derivedFrom":subQ2}),1.0]])]});}
            var Q18;
            {var subQ3=sQuery(id+"F5.wireOp",EDGE,"E82.MirrorCS");Q18=makeQuery(id+"F5.imprint","IMPRINT",FACE,{"disambiguationData":[TD([[makeQuery(id+"F5.imprint","IMPRINT",EDGE,{"derivedFrom":subQ3}),-1.0]])]});}
            var Q19;
            {var subQ3=sQuery(id+"F5.wireOp",EDGE,"E82.MirrorCS");Q19=makeQuery(id+"F5.imprint","IMPRINT",FACE,{"disambiguationData":[TD([[makeQuery(id+"F5.imprint","IMPRINT",EDGE,{"derivedFrom":subQ3}),1.0]])]});}
            extrude(context, id + "F7", {"entities" : qUnion([Q0, Q1, Q2, Q3, Q4, Q5, Q6, Q7, Q8, Q9, Q10, Q11, Q12, Q13, Q14, Q15, Q16, Q17, Q18, Q19]), "operationType" : NewBodyOperationType.REMOVE, "endBound" : BoundingType.THROUGH_ALL, "oppositeDirection" : true, "depth" : 25 * mm, "offsetDistance" : 25 * mm});
        }
        {
            var Q0;
            Q0=qCreatedBy(makeId("Front.planeOp"),FACE);
            var sketch = newSketch(context, id + "F8", { "sketchPlane" : qUnion([Q0])});
            skLineSegment(sketch, "E83.bottom", {"start": v(-219.07, -44.05) * mm, "end": v(219.07, -44.05) * mm});
            skLineSegment(sketch, "E83.top", {"start": v(-219.07, 44.05) * mm, "end": v(219.07, 44.05) * mm});
            skLineSegment(sketch, "E83.left", {"start": v(-219.07, -44.05) * mm, "end": v(-219.07, 44.05) * mm});
            skLineSegment(sketch, "E83.right", {"start": v(219.07, -44.05) * mm, "end": v(219.07, 44.05) * mm});
            skPoint(sketch, "E83.middle", {"position": v(0, 0) * mm});
            skSolve(sketch);
        }
        {
            var Q0;
            Q0=makeQuery(id+"F8.imprint","IMPRINT",FACE,{"disambiguationData":[TD([[makeQuery(id+"F8.imprint","IMPRINT",EDGE,{"derivedFrom":sQuery(id+"F8.wireOp",EDGE,"E83.bottom")}),1.0]])]});
            extrude(context, id + "F9", {"entities" : qUnion([Q0]), "oppositeDirection" : true, "depth" : 141.44 * mm, "offsetDistance" : 25 * mm});
        }
        {
            var Q0;
            Q0=makeQuery(id+"F9.opExtrude","CAP_FACE",FACE,{"disambiguationData":[OSD([sQuery(id+"F8.wireOp",EDGE,"E83.bottom"),sQuery(id+"F8.wireOp",EDGE,"E83.top"),sQuery(id+"F8.wireOp",EDGE,"E83.left"),sQuery(id+"F8.wireOp",EDGE,"E83.right")])],"isStart":false});
            var sketch = newSketch(context, id + "F10", { "sketchPlane" : qUnion([Q0])});
            skCircle(sketch, "E84", {"center": v(-207.4, 20.94) * mm, "radius": 1.75 * mm});
            skCircle(sketch, "E85.1.0.0", {"center": v(-141.35, 20.94) * mm, "radius": 1.75 * mm});
            skLineSegment(sketch, "E85.direction1", {"start": v(-207.4, 20.94) * mm, "end": v(-141.35, 20.94) * mm, "construction": true});
            skLineSegment(sketch, "E86.1.0.0", {"start": v(-135.76, 20.94) * mm, "end": v(-69.72, 20.94) * mm, "construction": true});
            skCircle(sketch, "E86.1.0.1", {"center": v(-69.72, 20.94) * mm, "radius": 1.75 * mm});
            skCircle(sketch, "E86.1.0.2", {"center": v(-135.76, 20.94) * mm, "radius": 1.75 * mm});
            skLineSegment(sketch, "E86.2.0.0", {"start": v(-64.13, 20.94) * mm, "end": v(1.9, 20.94) * mm, "construction": true});
            skCircle(sketch, "E86.2.0.1", {"center": v(1.9, 20.94) * mm, "radius": 1.75 * mm});
            skCircle(sketch, "E86.2.0.2", {"center": v(-64.13, 20.94) * mm, "radius": 1.75 * mm});
            skLineSegment(sketch, "E86.direction1", {"start": v(-207.4, 20.94) * mm, "end": v(-135.76, 20.94) * mm, "construction": true});
            skCircle(sketch, "E87", {"center": v(7.5, 20.94) * mm, "radius": 1.75 * mm});
            skCircle(sketch, "E88", {"center": v(53.21, 20.94) * mm, "radius": 1.75 * mm});
            skCircle(sketch, "E89.1.0.0", {"center": v(104.52, 20.94) * mm, "radius": 1.75 * mm});
            skCircle(sketch, "E89.1.0.1", {"center": v(58.8, 20.94) * mm, "radius": 1.75 * mm});
            skCircle(sketch, "E89.2.0.0", {"center": v(155.83, 20.94) * mm, "radius": 1.75 * mm});
            skCircle(sketch, "E89.2.0.1", {"center": v(110.1, 20.94) * mm, "radius": 1.75 * mm});
            skCircle(sketch, "E89.3.0.0", {"center": v(207.14, 20.94) * mm, "radius": 1.75 * mm});
            skCircle(sketch, "E89.3.0.1", {"center": v(161.42, 20.94) * mm, "radius": 1.75 * mm});
            skLineSegment(sketch, "E89.direction1", {"start": v(7.5, 20.94) * mm, "end": v(58.8, 20.94) * mm, "construction": true});
            skCircle(sketch, "E90", {"center": v(-202.82, -26.04) * mm, "radius": 1.75 * mm});
            skCircle(sketch, "E91", {"center": v(-157.1, -26.04) * mm, "radius": 1.75 * mm});
            skCircle(sketch, "E92.1.0.0", {"center": v(-151.51, -26.04) * mm, "radius": 1.75 * mm});
            skCircle(sketch, "E92.1.0.1", {"center": v(-105.8, -26.04) * mm, "radius": 1.75 * mm});
            skCircle(sketch, "E92.2.0.0", {"center": v(-100.2, -26.04) * mm, "radius": 1.75 * mm});
            skCircle(sketch, "E92.2.0.1", {"center": v(-54.48, -26.04) * mm, "radius": 1.75 * mm});
            skCircle(sketch, "E92.3.0.0", {"center": v(-48.9, -26.04) * mm, "radius": 1.75 * mm});
            skCircle(sketch, "E92.3.0.1", {"center": v(-3.18, -26.04) * mm, "radius": 1.75 * mm});
            skLineSegment(sketch, "E92.direction1", {"start": v(-202.82, -26.04) * mm, "end": v(-151.51, -26.04) * mm, "construction": true});
            skCircle(sketch, "E93", {"center": v(209.42, -26.03) * mm, "radius": 1.75 * mm});
            skCircle(sketch, "E94", {"center": v(163.7, -26.03) * mm, "radius": 1.75 * mm});
            skSolve(sketch);
        }
        {
            var Q0;
            Q0 = qSketchRegion(id + "F10", true);
            extrude(context, id + "F11", {"entities" : qUnion([Q0]), "operationType" : NewBodyOperationType.REMOVE, "oppositeDirection" : true, "depth" : 1 * mm, "offsetDistance" : 25 * mm});
        }
        {
            var Q0;
            Q0=makeQuery(id+"F9.opExtrude","CAP_FACE",FACE,{"disambiguationData":[OSD([sQuery(id+"F8.wireOp",EDGE,"E83.bottom"),sQuery(id+"F8.wireOp",EDGE,"E83.top"),sQuery(id+"F8.wireOp",EDGE,"E83.left"),sQuery(id+"F8.wireOp",EDGE,"E83.right")])],"isStart":false});
            var sketch = newSketch(context, id + "F12", { "sketchPlane" : qUnion([Q0])});
            skCircle(sketch, "E95", {"center": v(210.95, -5.95) * mm, "radius": 4.06 * mm});
            skCircle(sketch, "E96.cCircle", {"center": v(210.95, -5.95) * mm, "radius": 2.95 * mm, "construction": true});
            skLineSegment(sketch, "E96.0", {"start": v(214.2, -6.97) * mm, "end": v(211.69, -9.27) * mm});
            skLineSegment(sketch, "E96.1", {"start": v(211.69, -9.27) * mm, "end": v(208.44, -8.25) * mm});
            skLineSegment(sketch, "E96.2", {"start": v(208.44, -8.25) * mm, "end": v(207.7, -4.93) * mm});
            skLineSegment(sketch, "E96.3", {"start": v(207.7, -4.93) * mm, "end": v(210.2, -2.63) * mm});
            skLineSegment(sketch, "E96.4", {"start": v(210.2, -2.63) * mm, "end": v(213.45, -3.65) * mm});
            skLineSegment(sketch, "E96.5", {"start": v(213.45, -3.65) * mm, "end": v(214.2, -6.97) * mm});
            skPoint(sketch, "E96.0.midPoint", {"position": v(212.94, -8.12) * mm});
            skSolve(sketch);
        }
        {
            var Q0;
            Q0=makeQuery(id+"F12.imprint","IMPRINT",FACE,{"disambiguationData":[TD([[makeQuery(id+"F12.imprint","IMPRINT",EDGE,{"derivedFrom":sQuery(id+"F12.wireOp",EDGE,"E95")}),1.0]])]});
            extrude(context, id + "F13", {"entities" : qUnion([Q0]), "operationType" : NewBodyOperationType.ADD, "depth" : 1.2 * mm, "offsetDistance" : 25 * mm});
        }
        {
            var Q0;
            Q0=makeQuery(id+"F12.imprint","IMPRINT",FACE,{"disambiguationData":[TD([[makeQuery(id+"F12.imprint","IMPRINT",EDGE,{"derivedFrom":sQuery(id+"F12.wireOp",EDGE,"E96.0")}),-1.0]])]});
            extrude(context, id + "F14", {"entities" : qUnion([Q0]), "operationType" : NewBodyOperationType.ADD, "depth" : 4 * mm, "offsetDistance" : 25 * mm});
        }
        {
            var Q0;
            Q0=makeQuery(id+"F14.opExtrude","CAP_FACE",FACE,{"disambiguationData":[OSD([sQuery(id+"F12.wireOp",EDGE,"E96.0"),sQuery(id+"F12.wireOp",EDGE,"E96.1"),sQuery(id+"F12.wireOp",EDGE,"E96.2"),sQuery(id+"F12.wireOp",EDGE,"E96.3"),sQuery(id+"F12.wireOp",EDGE,"E96.4"),sQuery(id+"F12.wireOp",EDGE,"E96.5")])],"isStart":false});
            var Q1;
            Q1=makeQuery(id+"F13.opExtrude","CAP_FACE",FACE,{"disambiguationData":[OSD([sQuery(id+"F12.wireOp",EDGE,"E95"),sQuery(id+"F12.wireOp",EDGE,"E96.0"),sQuery(id+"F12.wireOp",EDGE,"E96.1"),sQuery(id+"F12.wireOp",EDGE,"E96.2"),sQuery(id+"F12.wireOp",EDGE,"E96.3"),sQuery(id+"F12.wireOp",EDGE,"E96.4"),sQuery(id+"F12.wireOp",EDGE,"E96.5")])],"isStart":false});
            chamfer(context, id + "F15", {"entities" : qUnion([Q0, Q1]), "width" : 0.2 * mm, "tangentPropagation" : true});
        }
        {
            var Q0;
            Q0=makeQuery(id+"F12.imprint","IMPRINT",FACE,{"disambiguationData":[TD([[makeQuery(id+"F12.imprint","IMPRINT",EDGE,{"derivedFrom":sQuery(id+"F12.wireOp",EDGE,"E95")}),-1.0]])]});
            var sketch = newSketch(context, id + "F16", { "sketchPlane" : qUnion([Q0])});
            skCircle(sketch, "E97", {"center": v(146.18, -6.71) * mm, "radius": 4.83 * mm});
            skCircle(sketch, "E98", {"center": v(146.18, -6.71) * mm, "radius": 4.58 * mm});
            skCircle(sketch, "E99", {"center": v(146.18, -6.71) * mm, "radius": 1.65 * mm});
            skCircle(sketch, "E100.0.1.0", {"center": v(146.18, -22.97) * mm, "radius": 4.83 * mm});
            skCircle(sketch, "E100.0.1.1", {"center": v(146.18, -22.97) * mm, "radius": 4.58 * mm});
            skCircle(sketch, "E100.0.1.2", {"center": v(146.18, -22.97) * mm, "radius": 1.65 * mm});
            skLineSegment(sketch, "E100.direction1", {"start": v(146.18, -6.71) * mm, "end": v(171.18, -6.71) * mm, "construction": true});
            skLineSegment(sketch, "E100.direction2", {"start": v(146.18, -6.71) * mm, "end": v(146.18, -22.97) * mm, "construction": true});
            skSolve(sketch);
        }
        {
            var Q0;
            Q0=makeQuery(id+"F16.imprint","IMPRINT",FACE,{"disambiguationData":[TD([[makeQuery(id+"F16.imprint","IMPRINT",EDGE,{"derivedFrom":sQuery(id+"F16.wireOp",EDGE,"E97")}),1.0]])]});
            var Q1;
            Q1=makeQuery(id+"F16.imprint","IMPRINT",FACE,{"disambiguationData":[TD([[makeQuery(id+"F16.imprint","IMPRINT",EDGE,{"derivedFrom":sQuery(id+"F16.wireOp",EDGE,"E99")}),1.0]])]});
            var Q2;
            Q2=makeQuery(id+"F16.imprint","IMPRINT",FACE,{"disambiguationData":[TD([[makeQuery(id+"F16.imprint","IMPRINT",EDGE,{"derivedFrom":sQuery(id+"F16.wireOp",EDGE,"E100.0.1.2")}),1.0]])]});
            var Q3;
            Q3=makeQuery(id+"F16.imprint","IMPRINT",FACE,{"disambiguationData":[TD([[makeQuery(id+"F16.imprint","IMPRINT",EDGE,{"derivedFrom":sQuery(id+"F16.wireOp",EDGE,"E100.0.1.0")}),1.0]])]});
            extrude(context, id + "F17", {"entities" : qUnion([Q0, Q1, Q2, Q3]), "operationType" : NewBodyOperationType.ADD, "depth" : 10 * mm, "offsetDistance" : 25 * mm});
        }
        {
            var Q0;
            Q0=makeQuery(id+"F12.imprint","IMPRINT",FACE,{"disambiguationData":[TD([[makeQuery(id+"F12.imprint","IMPRINT",EDGE,{"derivedFrom":sQuery(id+"F12.wireOp",EDGE,"E95")}),-1.0]])]});
            var sketch = newSketch(context, id + "F18", { "sketchPlane" : qUnion([Q0])});
            skLineSegment(sketch, "E101", {"start": v(9.24, -26.83) * mm, "end": v(9.24, -19.2) * mm});
            skLineSegment(sketch, "E102", {"start": v(9.24, -19.2) * mm, "end": v(11.78, -19.2) * mm});
            skLineSegment(sketch, "E103", {"start": v(11.78, -19.2) * mm, "end": v(11.78, -17.94) * mm});
            skLineSegment(sketch, "E104", {"start": v(11.78, -17.94) * mm, "end": v(13.81, -17.94) * mm});
            skLineSegment(sketch, "E105", {"start": v(13.81, -17.94) * mm, "end": v(13.81, -17.17) * mm});
            skLineSegment(sketch, "E106", {"start": v(13.81, -17.17) * mm, "end": v(17.62, -17.17) * mm});
            skLineSegment(sketch, "E107", {"start": v(17.62, -17.17) * mm, "end": v(17.62, -17.94) * mm});
            skLineSegment(sketch, "E108", {"start": v(17.62, -17.94) * mm, "end": v(19.66, -17.94) * mm});
            skLineSegment(sketch, "E109", {"start": v(19.66, -17.94) * mm, "end": v(19.66, -19.2) * mm});
            skLineSegment(sketch, "E110", {"start": v(19.66, -19.2) * mm, "end": v(22.2, -19.2) * mm});
            skLineSegment(sketch, "E111", {"start": v(22.2, -19.2) * mm, "end": v(22.2, -26.83) * mm});
            skLineSegment(sketch, "E112", {"start": v(22.2, -26.83) * mm, "end": v(9.24, -26.83) * mm});
            skLineSegment(sketch, "E113.bottom", {"start": v(7.97, -29.83) * mm, "end": v(23.47, -29.83) * mm});
            skLineSegment(sketch, "E113.top", {"start": v(7.97, -16.41) * mm, "end": v(23.47, -16.41) * mm});
            skLineSegment(sketch, "E113.left", {"start": v(7.97, -29.83) * mm, "end": v(7.97, -16.41) * mm});
            skLineSegment(sketch, "E113.right", {"start": v(23.47, -29.83) * mm, "end": v(23.47, -16.41) * mm});
            skLineSegment(sketch, "E114.1.0.0", {"start": v(33.37, -29.83) * mm, "end": v(48.87, -29.83) * mm});
            skLineSegment(sketch, "E114.1.0.1", {"start": v(47.6, -26.83) * mm, "end": v(34.64, -26.83) * mm});
            skLineSegment(sketch, "E114.1.0.2", {"start": v(47.6, -19.2) * mm, "end": v(47.6, -26.83) * mm});
            skLineSegment(sketch, "E114.1.0.3", {"start": v(33.37, -29.83) * mm, "end": v(33.37, -16.41) * mm});
            skLineSegment(sketch, "E114.1.0.4", {"start": v(48.87, -29.83) * mm, "end": v(48.87, -16.41) * mm});
            skLineSegment(sketch, "E114.1.0.5", {"start": v(34.64, -26.83) * mm, "end": v(34.64, -19.2) * mm});
            skLineSegment(sketch, "E114.1.0.6", {"start": v(33.37, -16.41) * mm, "end": v(48.87, -16.41) * mm});
            skLineSegment(sketch, "E114.1.0.7", {"start": v(39.21, -17.17) * mm, "end": v(43.02, -17.17) * mm});
            skLineSegment(sketch, "E114.1.0.8", {"start": v(34.64, -19.2) * mm, "end": v(37.18, -19.2) * mm});
            skLineSegment(sketch, "E114.1.0.9", {"start": v(45.06, -19.2) * mm, "end": v(47.6, -19.2) * mm});
            skLineSegment(sketch, "E114.1.0.10", {"start": v(37.18, -17.94) * mm, "end": v(39.21, -17.94) * mm});
            skLineSegment(sketch, "E114.1.0.11", {"start": v(39.21, -17.94) * mm, "end": v(39.21, -17.17) * mm});
            skLineSegment(sketch, "E114.1.0.12", {"start": v(43.02, -17.94) * mm, "end": v(45.06, -17.94) * mm});
            skLineSegment(sketch, "E114.1.0.13", {"start": v(37.18, -19.2) * mm, "end": v(37.18, -17.94) * mm});
            skLineSegment(sketch, "E114.1.0.14", {"start": v(45.06, -17.94) * mm, "end": v(45.06, -19.2) * mm});
            skLineSegment(sketch, "E114.1.0.15", {"start": v(43.02, -17.17) * mm, "end": v(43.02, -17.94) * mm});
            skLineSegment(sketch, "E114.direction1", {"start": v(7.97, -29.83) * mm, "end": v(33.37, -29.83) * mm, "construction": true});
            skSolve(sketch);
        }
        {
            var Q0;
            Q0=makeQuery(id+"F18.imprint","IMPRINT",FACE,{"disambiguationData":[TD([[makeQuery(id+"F18.imprint","IMPRINT",EDGE,{"derivedFrom":sQuery(id+"F18.wireOp",EDGE,"E101")}),-1.0]])]});
            var Q1;
            Q1=makeQuery(id+"F18.imprint","IMPRINT",FACE,{"disambiguationData":[TD([[makeQuery(id+"F18.imprint","IMPRINT",EDGE,{"derivedFrom":sQuery(id+"F18.wireOp",EDGE,"E114.1.0.1")}),-1.0]])]});
            extrude(context, id + "F19", {"entities" : qUnion([Q0, Q1]), "operationType" : NewBodyOperationType.REMOVE, "oppositeDirection" : true, "depth" : 15 * mm, "offsetDistance" : 25 * mm});
        }
        {
            var Q0;
            Q0=makeQuery(id+"F18.imprint","IMPRINT",FACE,{"disambiguationData":[TD([[makeQuery(id+"F18.imprint","IMPRINT",EDGE,{"derivedFrom":sQuery(id+"F18.wireOp",EDGE,"E101")}),1.0]])]});
            var Q1;
            Q1=makeQuery(id+"F18.imprint","IMPRINT",FACE,{"disambiguationData":[TD([[makeQuery(id+"F18.imprint","IMPRINT",EDGE,{"derivedFrom":sQuery(id+"F18.wireOp",EDGE,"E114.1.0.0")}),1.0]])]});
            extrude(context, id + "F20", {"entities" : qUnion([Q0, Q1]), "operationType" : NewBodyOperationType.ADD, "depth" : 0.2 * mm, "offsetDistance" : 25 * mm});
        }
        {
            var Q0;
            Q0=makeQuery(id+"F18.imprint","IMPRINT",FACE,{"disambiguationData":[TD([[makeQuery(id+"F18.imprint","IMPRINT",EDGE,{"derivedFrom":sQuery(id+"F18.wireOp",EDGE,"E113.bottom")}),-1.0]])]});
            var sketch = newSketch(context, id + "F21", { "sketchPlane" : qUnion([Q0])});
            skCircle(sketch, "E115.cCircle", {"center": v(67.7, -23.24) * mm, "radius": 2.35 * mm, "construction": true});
            skLineSegment(sketch, "E115.0", {"start": v(69.69, -25.08) * mm, "end": v(67.1, -25.89) * mm});
            skLineSegment(sketch, "E115.1", {"start": v(67.1, -25.89) * mm, "end": v(65.1, -24.05) * mm});
            skLineSegment(sketch, "E115.2", {"start": v(65.1, -24.05) * mm, "end": v(65.7, -21.4) * mm});
            skLineSegment(sketch, "E115.3", {"start": v(65.7, -21.4) * mm, "end": v(68.29, -20.6) * mm});
            skLineSegment(sketch, "E115.4", {"start": v(68.29, -20.6) * mm, "end": v(70.28, -22.43) * mm});
            skLineSegment(sketch, "E115.5", {"start": v(70.28, -22.43) * mm, "end": v(69.69, -25.08) * mm});
            skPoint(sketch, "E115.0.midPoint", {"position": v(68.39, -25.48) * mm});
            skCircle(sketch, "E116.cCircle", {"center": v(93.1, -23.24) * mm, "radius": 2.35 * mm, "construction": true});
            skLineSegment(sketch, "E116.0", {"start": v(95.17, -24.99) * mm, "end": v(92.62, -25.91) * mm});
            skLineSegment(sketch, "E116.1", {"start": v(92.62, -25.91) * mm, "end": v(90.54, -24.17) * mm});
            skLineSegment(sketch, "E116.2", {"start": v(90.54, -24.17) * mm, "end": v(91.01, -21.5) * mm});
            skLineSegment(sketch, "E116.3", {"start": v(91.01, -21.5) * mm, "end": v(93.56, -20.57) * mm});
            skLineSegment(sketch, "E116.4", {"start": v(93.56, -20.57) * mm, "end": v(95.64, -22.31) * mm});
            skLineSegment(sketch, "E116.5", {"start": v(95.64, -22.31) * mm, "end": v(95.17, -24.99) * mm});
            skPoint(sketch, "E116.0.midPoint", {"position": v(93.9, -25.45) * mm});
            skPoint(sketch, "E117.1.0.0", {"position": v(128.18, -25.45) * mm});
            skPoint(sketch, "E117.1.0.1", {"position": v(102.68, -25.48) * mm});
            skLineSegment(sketch, "E117.1.0.2", {"start": v(99.99, -21.4) * mm, "end": v(102.58, -20.6) * mm});
            skLineSegment(sketch, "E117.1.0.3", {"start": v(101.38, -25.89) * mm, "end": v(99.4, -24.05) * mm});
            skCircle(sketch, "E117.1.0.4", {"center": v(101.98, -23.24) * mm, "radius": 2.35 * mm, "construction": true});
            skLineSegment(sketch, "E117.1.0.5", {"start": v(103.98, -25.08) * mm, "end": v(101.38, -25.89) * mm});
            skLineSegment(sketch, "E117.1.0.6", {"start": v(99.4, -24.05) * mm, "end": v(99.99, -21.4) * mm});
            skLineSegment(sketch, "E117.1.0.7", {"start": v(129.93, -22.31) * mm, "end": v(129.46, -24.99) * mm});
            skLineSegment(sketch, "E117.1.0.8", {"start": v(102.58, -20.6) * mm, "end": v(104.57, -22.43) * mm});
            skLineSegment(sketch, "E117.1.0.9", {"start": v(104.57, -22.43) * mm, "end": v(103.98, -25.08) * mm});
            skCircle(sketch, "E117.1.0.10", {"center": v(127.38, -23.24) * mm, "radius": 2.35 * mm, "construction": true});
            skLineSegment(sketch, "E117.1.0.11", {"start": v(129.46, -24.99) * mm, "end": v(126.9, -25.91) * mm});
            skLineSegment(sketch, "E117.1.0.12", {"start": v(126.9, -25.91) * mm, "end": v(124.83, -24.17) * mm});
            skLineSegment(sketch, "E117.1.0.13", {"start": v(124.83, -24.17) * mm, "end": v(125.3, -21.5) * mm});
            skLineSegment(sketch, "E117.1.0.14", {"start": v(125.3, -21.5) * mm, "end": v(127.85, -20.57) * mm});
            skLineSegment(sketch, "E117.1.0.15", {"start": v(127.85, -20.57) * mm, "end": v(129.93, -22.31) * mm});
            skLineSegment(sketch, "E117.direction1", {"start": v(65.1, -24.05) * mm, "end": v(99.4, -24.05) * mm, "construction": true});
            skCircle(sketch, "E118", {"center": v(67.7, -23.24) * mm, "radius": 1.25 * mm});
            skCircle(sketch, "E119", {"center": v(93.1, -23.24) * mm, "radius": 1.25 * mm});
            skCircle(sketch, "E120", {"center": v(101.98, -23.24) * mm, "radius": 1.25 * mm});
            skCircle(sketch, "E121", {"center": v(127.38, -23.24) * mm, "radius": 1.25 * mm});
            skSolve(sketch);
        }
        {
            var Q0;
            Q0 = qSketchRegion(id + "F21", true);
            extrude(context, id + "F22", {"entities" : qUnion([Q0]), "operationType" : NewBodyOperationType.ADD, "depth" : 4.6 * mm, "offsetDistance" : 25 * mm});
        }
        {
            var Q0;
            Q0=makeQuery(id+"F1.opExtrude","CAP_FACE",FACE,{"disambiguationData":[OSD([sQuery(id+"F0.wireOp",EDGE,"E0.top"),sQuery(id+"F0.wireOp",EDGE,"E0.left"),sQuery(id+"F0.wireOp",EDGE,"E0.right"),sQuery(id+"F0.wireOp",EDGE,"E2"),sQuery(id+"F0.wireOp",EDGE,"E3"),sQuery(id+"F0.wireOp",EDGE,"E5.MirrorCS"),sQuery(id+"F0.wireOp",EDGE,"E6.MirrorCS"),sQuery(id+"F0.wireOp",EDGE,"E7.MirrorCS"),sQuery(id+"F0.wireOp",EDGE,"E8.MirrorCS"),sQuery(id+"F0.wireOp",EDGE,"E9.MirrorCS"),sQuery(id+"F0.wireOp",EDGE,"E10.MirrorCS"),sQuery(id+"F0.wireOp",EDGE,"E0.bottom")])],"isStart":false});
            var sketch = newSketch(context, id + "F23", { "sketchPlane" : qUnion([Q0])});
            skLineSegment(sketch, "E122.bottom", {"start": v(-202.5, -5.46) * mm, "end": v(16.06, -5.46) * mm});
            skLineSegment(sketch, "E122.top", {"start": v(-202.5, -37.72) * mm, "end": v(16.06, -37.72) * mm});
            skLineSegment(sketch, "E122.left", {"start": v(-206, -8.96) * mm, "end": v(-206, -34.22) * mm});
            skLineSegment(sketch, "E122.right", {"start": v(19.56, -8.96) * mm, "end": v(19.56, -34.22) * mm});
            skPoint(sketch, "E123.visualSharp", {"position": v(-206, -5.46) * mm});
            skArc(sketch, "E123.filletArc", {"start": v(-202.5, -5.46) * mm, "mid": v(-204.97, -6.49) * mm, "end": v(-206, -8.96) * mm});
            skPoint(sketch, "E124.visualSharp", {"position": v(19.56, -5.46) * mm});
            skArc(sketch, "E124.filletArc", {"start": v(19.56, -8.96) * mm, "mid": v(18.53, -6.49) * mm, "end": v(16.06, -5.46) * mm});
            skPoint(sketch, "E125.visualSharp", {"position": v(19.56, -37.72) * mm});
            skArc(sketch, "E125.filletArc", {"start": v(16.06, -37.72) * mm, "mid": v(18.53, -36.7) * mm, "end": v(19.56, -34.22) * mm});
            skPoint(sketch, "E126.visualSharp", {"position": v(-206, -37.72) * mm});
            skArc(sketch, "E126.filletArc", {"start": v(-206, -34.22) * mm, "mid": v(-204.97, -36.7) * mm, "end": v(-202.5, -37.72) * mm});
            skLineSegment(sketch, "E127.bottom", {"start": v(-202.5, -5.96) * mm, "end": v(16.06, -5.96) * mm});
            skLineSegment(sketch, "E127.top", {"start": v(-202.5, -37.22) * mm, "end": v(16.06, -37.22) * mm});
            skLineSegment(sketch, "E127.left", {"start": v(-205.5, -8.96) * mm, "end": v(-205.5, -34.22) * mm});
            skLineSegment(sketch, "E127.right", {"start": v(19.06, -8.96) * mm, "end": v(19.06, -34.22) * mm});
            skPoint(sketch, "E128.visualSharp", {"position": v(19.06, -37.22) * mm});
            skArc(sketch, "E128.filletArc", {"start": v(16.06, -37.22) * mm, "mid": v(18.18, -36.34) * mm, "end": v(19.06, -34.22) * mm});
            skPoint(sketch, "E129.visualSharp", {"position": v(19.06, -5.96) * mm});
            skArc(sketch, "E129.filletArc", {"start": v(19.06, -8.96) * mm, "mid": v(18.18, -6.84) * mm, "end": v(16.06, -5.96) * mm});
            skPoint(sketch, "E130.visualSharp", {"position": v(-205.5, -5.96) * mm});
            skArc(sketch, "E130.filletArc", {"start": v(-202.5, -5.96) * mm, "mid": v(-204.62, -6.84) * mm, "end": v(-205.5, -8.96) * mm});
            skPoint(sketch, "E131.visualSharp", {"position": v(-205.5, -37.22) * mm});
            skArc(sketch, "E131.filletArc", {"start": v(-205.5, -34.22) * mm, "mid": v(-204.62, -36.34) * mm, "end": v(-202.5, -37.22) * mm});
            skSolve(sketch);
        }
        {
            var Q0;
            Q0=makeQuery(id+"F23.imprint","IMPRINT",FACE,{"disambiguationData":[TD([[makeQuery(id+"F23.imprint","IMPRINT",EDGE,{"derivedFrom":sQuery(id+"F23.wireOp",EDGE,"E122.bottom")}),-1.0]])]});
            extrude(context, id + "F24", {"entities" : qUnion([Q0]), "depth" : 0.1 * mm, "offsetDistance" : 25 * mm});
        }
    });
